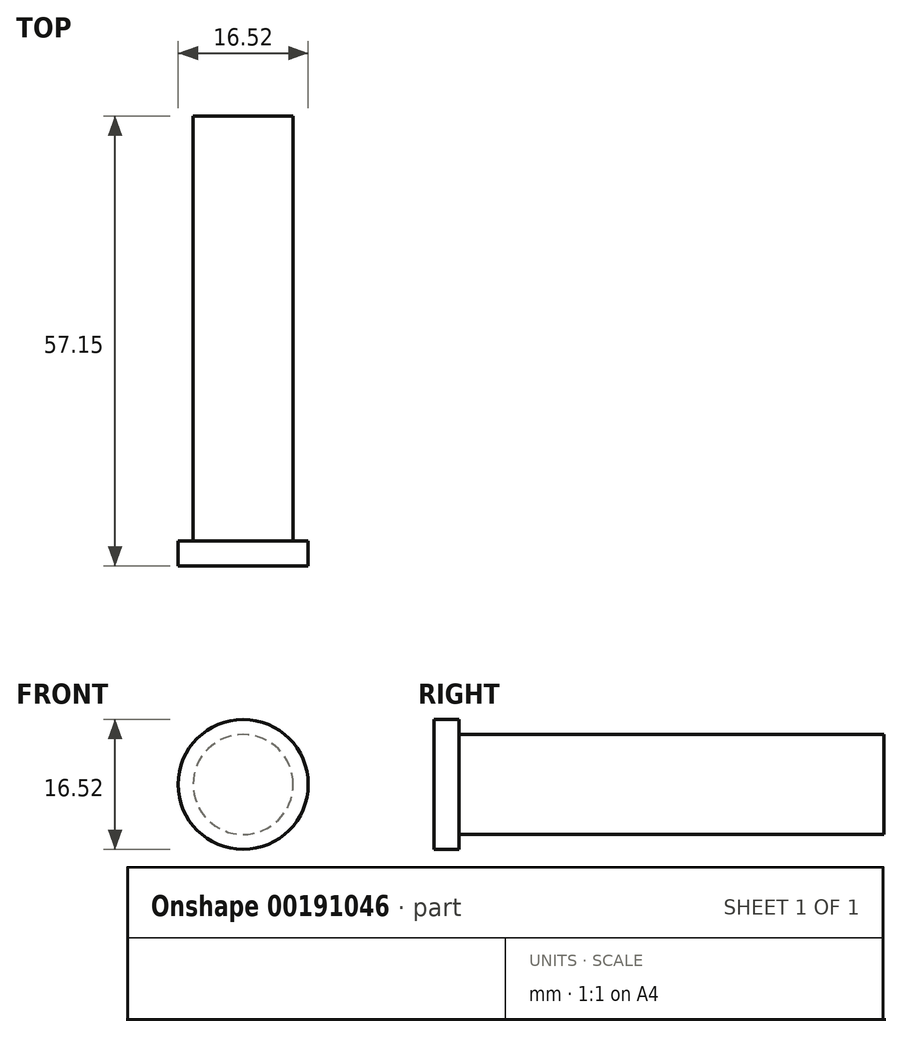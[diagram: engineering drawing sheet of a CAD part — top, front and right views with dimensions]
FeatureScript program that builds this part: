
annotation { "Feature Type Name" : "Feature", "Feature Type Description" : "" }
export const myFeature = defineFeature(function(context is Context, id is Id, definition is map)
    precondition{}
    {
        {
            var Q0;
            Q0=qCreatedBy(makeId("Front.planeOp"),FACE);
            var sketch = newSketch(context, id + "F0", { "sketchPlane" : qUnion([Q0])});
            skCircle(sketch, "E0", {"center": v(0, 0) * mm, "radius": 6.35 * mm});
            skSolve(sketch);
        }
        {
            var Q0;
            Q0 = qSketchRegion(id + "F0", true);
            extrude(context, id + "F1", {"entities" : qUnion([Q0]), "depth" : 57.15 * mm});
        }
        {
            var Q0;
            Q0=makeQuery(id+"F1.opExtrude","CAP_FACE",FACE,{"disambiguationData":[OSD([sQuery(id+"F0.wireOp",EDGE,"E0")])],"isStart":false});
            var sketch = newSketch(context, id + "F2", { "sketchPlane" : qUnion([Q0])});
            skCircle(sketch, "E1", {"center": v(0, 0) * mm, "radius": 8.26 * mm});
            skSolve(sketch);
        }
        {
            var Q0;
            Q0 = qSketchRegion(id + "F2", true);
            extrude(context, id + "F3", {"entities" : qUnion([Q0]), "operationType" : NewBodyOperationType.ADD, "oppositeDirection" : true, "depth" : 3.17 * mm});
        }
    });
